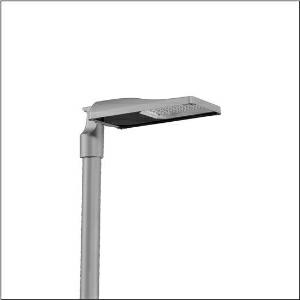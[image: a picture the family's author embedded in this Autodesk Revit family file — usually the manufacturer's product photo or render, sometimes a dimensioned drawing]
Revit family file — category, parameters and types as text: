
# Revit family: streetlight_sl_31_mini___st1_0a_5xh2d3ab08ha_5839
name_source: partatom
category: Lighting Fixtures
units: mm (PartAtom-declared; Revit-internal decimal feet)

## family parameters
Cut with Voids When Loaded = No
Host = Face
Light Source = No
Part Type = Normal
Room Calculation Point = No
Round Connector Dimension = Use Diameter
Shared = No

## types (1)
- --- (1 x LED, 9240 lm, 68.3 W, 3000K)
    Apparent Load = 68 VA
    CIE Flux Codes = 37 72 97 100 100
    Color Rendering = 70
    Color Temperature = 3000K
    Default Elevation = 1800 mm
    Description = Streetlight SL 31 mini Easy LST mast luminaire for post-top, side-entry; light control with lens of PMMA; light distribution: ST1.0a, direct asymmetric distribution, for standard-compliant lighting for roads and squares; LED: luminous flux: 9.240lm, light colour: 730, colour temperature: 3000K; luminous efficacy: 135,3lm/W; control: pre-setting: linear dimming characteristic, flexible luminous flux parameterisation, time-dependent luminous flux control, constant luminous flux control, power reduction, intelligent temperature release in ECG and LED module, overheat protection; luminaire housing, of diecast aluminium, SITECO metallic grey (DB 702S), corrosivity category C5 high according to DIN EN ISO 12944; cover of toughened safety glass, transparent, mast flange of diecast aluminium, SITECO metallic grey (DB 702S), spigot size: 76/60mm, mast flange included unmounted; cable length: 8,5m, connection cable pre-assembled; mains connection: 220..240V, AC, 50/60Hz; power consumption (at start of service life): 68,3W / (at end of service life): 74,8W / (with reduced operation 50%): 29,7W; protection rating (complete): IP66; insulation class (complete): insulation class II (safety insulation); impact resistance: IK10; certification: CE, ENEC, ENEC+, VDE, UKCA; permissible operating ambient temperature for outdoor applications: -40..+50°C; packaging unit: 1 piece

Light Distribution: ST1.0a
    Height = 76 mm
    Lamp = 1 x LED
    Lamp Light Flux = 9240 lm
    Lamp Power = 68.3 W
    Lamp count = 1
    Length = 547 mm
    Luminous efficacy = 135 lm/W
    Manufacturer = Siteco
    ModVariant = No
    Model = 5XH2D3AB08HA
    Number of Poles = 1
    OnlyDefault = Yes
    Power Factor = 1
    Product Name = Streetlight SL 31 mini | ST1.0a
    Product group = mast luminaire | pylon top
    ProductGroupID = 6100
    Protection Class = Protection class II
    Protection Degree = IP 66
    RLX_Detail_Level = 1
    RLX_Emergency_Light_Flux = 0 lm
    RLX_Emergency_Type = 0
    RLX_Emergency_Type_DB = No
    RlxData = <blob elided: 39381 chars, md5=f92d568e>
    Socket = socket
    Standby Power = 0 W
    System Light Flux = 9240 lm
    System Power = 68 W
    Type Comments = factory setting: luminous flux: 100 % | dim-lin: 254 | 693 mA
    Type Image = l_1300326.jpg
    URL = http://relux.com
    VarID = @adj_061613
    Voltage = 0 V
    Weight = 0.00 kg
    Width = 265 mm

## geometry (parser evidence)
native form markers: Blend x4, Sweep x11
no freeform markers — native parametric forms only
